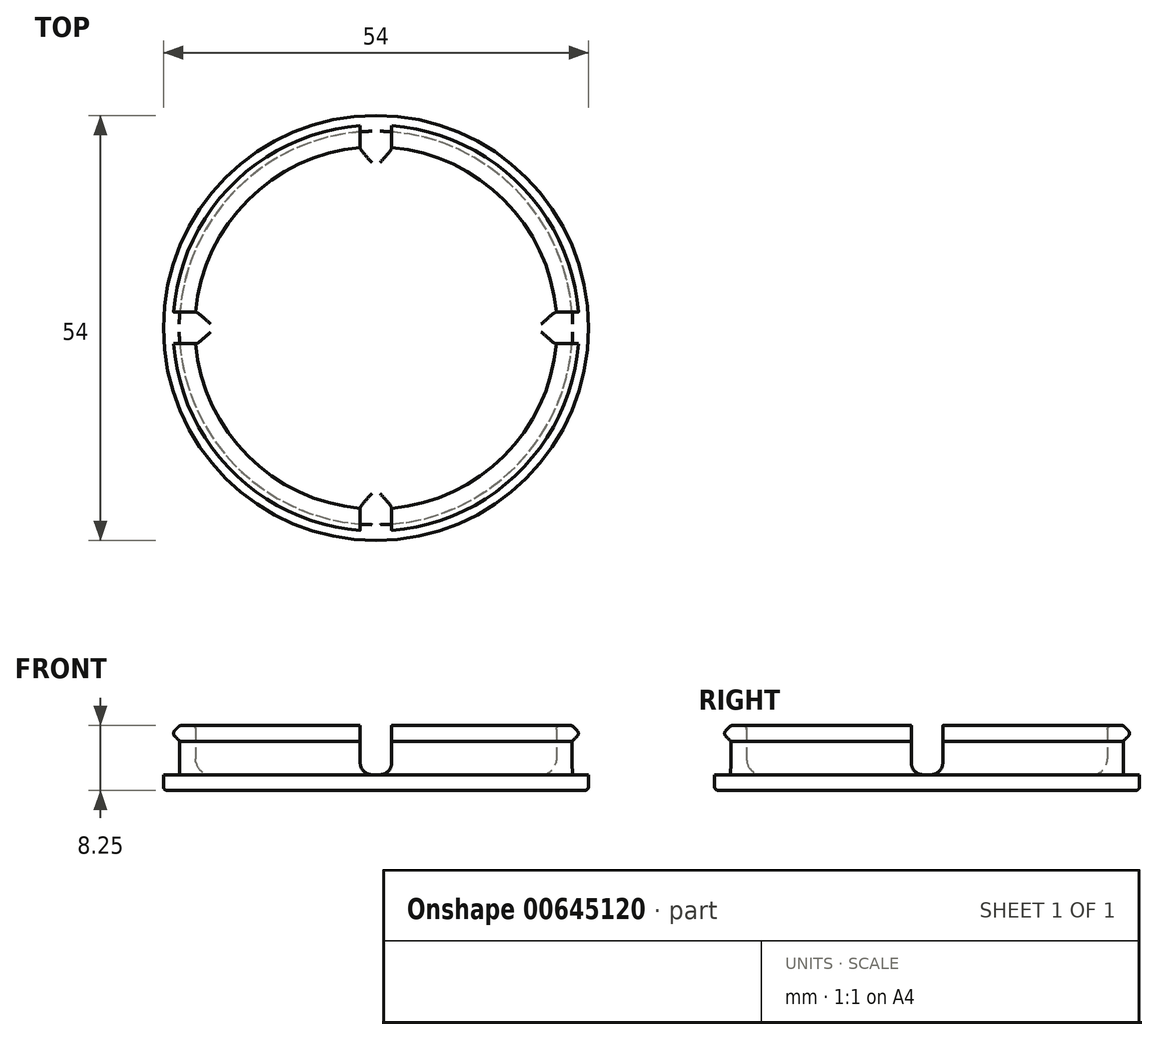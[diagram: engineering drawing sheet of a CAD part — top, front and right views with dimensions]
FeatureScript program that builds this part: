
annotation { "Feature Type Name" : "Feature", "Feature Type Description" : "" }
export const myFeature = defineFeature(function(context is Context, id is Id, definition is map)
    precondition{}
    {
        {
            var Q0;
            Q0=qCreatedBy(makeId("Front.planeOp"),FACE);
            var sketch = newSketch(context, id + "F0", { "sketchPlane" : qUnion([Q0])});
            skLineSegment(sketch, "E0", {"start": v(0, -39.03) * mm, "end": v(0, 63.1) * mm, "construction": true});
            skLineSegment(sketch, "E1", {"start": v(0, -2) * mm, "end": v(26.5, -2) * mm});
            skLineSegment(sketch, "E2", {"start": v(27, -1.5) * mm, "end": v(27, 0) * mm});
            skLineSegment(sketch, "E3", {"start": v(27, 0) * mm, "end": v(25, 0) * mm});
            skLineSegment(sketch, "E4", {"start": v(25, 0) * mm, "end": v(25, 4.25) * mm});
            skLineSegment(sketch, "E5", {"start": v(25, 4.25) * mm, "end": v(25.65, 4.9) * mm});
            skLineSegment(sketch, "E6", {"start": v(25.65, 5.6) * mm, "end": v(25.15, 6.1) * mm});
            skLineSegment(sketch, "E7", {"start": v(24.8, 6.25) * mm, "end": v(23.5, 6.25) * mm});
            skLineSegment(sketch, "E8", {"start": v(23, 5.75) * mm, "end": v(23, 2) * mm});
            skLineSegment(sketch, "E9", {"start": v(21, 0) * mm, "end": v(0, 0) * mm});
            skArc(sketch, "E10.filletArc", {"start": v(21, 0) * mm, "mid": v(22.41, 0.59) * mm, "end": v(23, 2) * mm});
            skPoint(sketch, "E11.visualSharp", {"position": v(27, -2) * mm});
            skArc(sketch, "E11.filletArc", {"start": v(26.5, -2) * mm, "mid": v(26.85, -1.85) * mm, "end": v(27, -1.5) * mm});
            skPoint(sketch, "E12.visualSharp", {"position": v(23, 6.25) * mm});
            skArc(sketch, "E12.filletArc", {"start": v(23.5, 6.25) * mm, "mid": v(23.15, 6.1) * mm, "end": v(23, 5.75) * mm});
            skPoint(sketch, "E13.visualSharp", {"position": v(26, 5.25) * mm});
            skArc(sketch, "E13.filletArc", {"start": v(25.65, 4.9) * mm, "mid": v(25.8, 5.25) * mm, "end": v(25.65, 5.6) * mm});
            skPoint(sketch, "E14.visualSharp", {"position": v(25, 6.25) * mm});
            skArc(sketch, "E14.filletArc", {"start": v(25.15, 6.1) * mm, "mid": v(24.98, 6.21) * mm, "end": v(24.8, 6.25) * mm});
            skLineSegment(sketch, "E15", {"start": v(0, -2) * mm, "end": v(0, 0) * mm});
            skSolve(sketch);
        }
        {
            var Q0;
            Q0 = qSketchRegion(id + "F0", true);
            var Q1;
            Q1=sQuery(id+"F0.wireOp",EDGE,"E0");
            revolve(context, id + "F1", {"entities" : qUnion([Q0]), "axis" : qUnion([Q1]), "revolveType" : RevolveType.FULL});
        }
        {
            var Q0;
            Q0=qCreatedBy(makeId("Front.planeOp"),FACE);
            var sketch = newSketch(context, id + "F2", { "sketchPlane" : qUnion([Q0])});
            skLineSegment(sketch, "E16", {"start": v(-2, 20) * mm, "end": v(-2, 1.5) * mm});
            skLineSegment(sketch, "E17", {"start": v(-0.5, 0) * mm, "end": v(0.5, 0) * mm});
            skLineSegment(sketch, "E18", {"start": v(2, 1.5) * mm, "end": v(2, 20) * mm});
            skLineSegment(sketch, "E19", {"start": v(2, 20) * mm, "end": v(-2, 20) * mm});
            skPoint(sketch, "E20.visualSharp", {"position": v(2, 0) * mm});
            skArc(sketch, "E20.filletArc", {"start": v(0.5, 0) * mm, "mid": v(1.56, 0.44) * mm, "end": v(2, 1.5) * mm});
            skPoint(sketch, "E21.visualSharp", {"position": v(-2, 0) * mm});
            skArc(sketch, "E21.filletArc", {"start": v(-2, 1.5) * mm, "mid": v(-1.56, 0.44) * mm, "end": v(-0.5, 0) * mm});
            skSolve(sketch);
        }
        {
            var Q0;
            Q0 = qSketchRegion(id + "F2", true);
            extrude(context, id + "F3", {"entities" : qUnion([Q0]), "operationType" : NewBodyOperationType.REMOVE, "endBound" : BoundingType.THROUGH_ALL, "depth" : 25 * mm, "offsetDistance" : 25 * mm, "hasSecondDirection" : true, "secondDirectionBound" : SecondDirectionBoundingType.THROUGH_ALL, "secondDirectionOppositeDirection" : true, "secondDirectionDepth" : 25 * mm});
        }
        {
            var Q0;
            Q0=qCreatedBy(makeId("Right.planeOp"),FACE);
            var sketch = newSketch(context, id + "F4", { "sketchPlane" : qUnion([Q0])});
            skLineSegment(sketch, "E22.bottom", {"start": v(2, 20) * mm, "end": v(-2, 20) * mm});
            skLineSegment(sketch, "E22.top", {"start": v(0.5, 0) * mm, "end": v(-0.5, 0) * mm});
            skLineSegment(sketch, "E22.left", {"start": v(2, 20) * mm, "end": v(2, 1.5) * mm});
            skLineSegment(sketch, "E22.right", {"start": v(-2, 20) * mm, "end": v(-2, 1.5) * mm});
            skPoint(sketch, "E23.visualSharp", {"position": v(2, 0) * mm});
            skArc(sketch, "E23.filletArc", {"start": v(0.5, 0) * mm, "mid": v(1.56, 0.44) * mm, "end": v(2, 1.5) * mm});
            skPoint(sketch, "E24.visualSharp", {"position": v(-2, 0) * mm});
            skArc(sketch, "E24.filletArc", {"start": v(-2, 1.5) * mm, "mid": v(-1.56, 0.44) * mm, "end": v(-0.5, 0) * mm});
            skSolve(sketch);
        }
        {
            var Q0;
            Q0 = qSketchRegion(id + "F4", true);
            extrude(context, id + "F5", {"entities" : qUnion([Q0]), "operationType" : NewBodyOperationType.REMOVE, "endBound" : BoundingType.THROUGH_ALL, "oppositeDirection" : true, "depth" : 25 * mm, "offsetDistance" : 25 * mm, "hasSecondDirection" : true, "secondDirectionBound" : SecondDirectionBoundingType.THROUGH_ALL, "secondDirectionOppositeDirection" : false, "secondDirectionDepth" : 25 * mm});
        }
    });
